# Revit family: KBB d=300_Precast-Console Beam_Spæncom
name_source: partatom
category: Structural Framing
revit_build: Autodesk Revit 2014 (Build: 20130308_1515(x64)
units: mm (PartAtom-declared; Revit-internal decimal feet)

## types (6) — shared parameters
Base width = 660 mm
Height console = 300 mm
Manufacturer = Spæncom
Model = KBB

## per-type parameters (varying)
| type | Height (bjælkekroppen) | Height element | Width (bjælkekroppen) | Width console |
| KBB 108/78 (150mm hylde) | 780 mm  [stored 2.55906 ft] | 1080 mm  [stored 3.54331 ft] | 435 mm  [stored 1.42717 ft] | 150 mm |
| KBB 108/78 (200mm hylde) | 780 mm  [stored 2.55906 ft] | 1080 mm  [stored 3.54331 ft] | 335 mm  [stored 1.09908 ft] | 200 mm  [stored 0.656168 ft] |
| KBB 120/90 (150mm hylde) | 900 mm  [stored 2.95276 ft] | 1200 mm | 435 mm  [stored 1.42717 ft] | 150 mm |
| KBB 120/90 (200mm hylde) | 900 mm  [stored 2.95276 ft] | 1200 mm | 335 mm  [stored 1.09908 ft] | 200 mm  [stored 0.656168 ft] |
| KBB 132/102 (150mm hylde) | 1020 mm  [stored 3.34646 ft] | 1320 mm | 435 mm  [stored 1.42717 ft] | 150 mm |
| KBB132/102 (200mm hylde) | 1020 mm  [stored 3.34646 ft] | 1320 mm | 335 mm  [stored 1.09908 ft] | 200 mm  [stored 0.656168 ft] |

note: [stored X ft] marks values corroborated as IEEE doubles in the binary element streams (Revit-internal decimal feet)

## geometry (parser evidence)
native form markers: Sweep x1
no freeform markers — native parametric forms only
